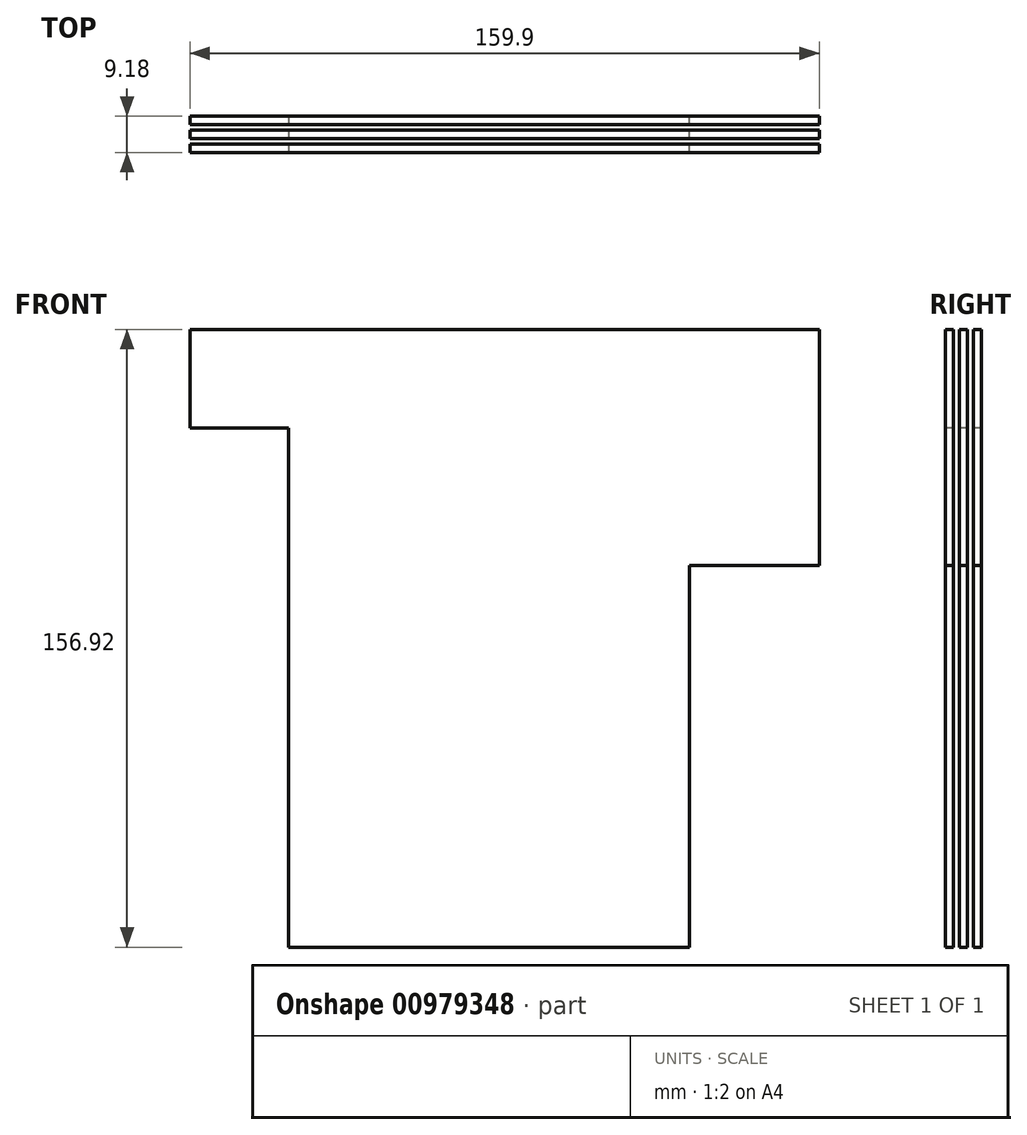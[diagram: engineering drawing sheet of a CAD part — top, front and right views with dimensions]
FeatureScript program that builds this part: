
annotation { "Feature Type Name" : "Feature", "Feature Type Description" : "" }
export const myFeature = defineFeature(function(context is Context, id is Id, definition is map)
    precondition{}
    {
        {
            var Q0;
            Q0=qCreatedBy(makeId("Top.planeOp"),FACE);
            var sketch = newSketch(context, id + "F0", { "sketchPlane" : qUnion([Q0])});
            skLineSegment(sketch, "E0.bottom", {"start": v(50.95, -1.03) * mm, "end": v(-50.95, -1.03) * mm});
            skLineSegment(sketch, "E0.top", {"start": v(50.95, 1.03) * mm, "end": v(-50.95, 1.03) * mm});
            skLineSegment(sketch, "E0.left", {"start": v(50.95, -1.03) * mm, "end": v(50.95, 1.03) * mm});
            skLineSegment(sketch, "E0.right", {"start": v(-50.95, -1.03) * mm, "end": v(-50.95, 1.03) * mm});
            skPoint(sketch, "E0.middle", {"position": v(0, 0) * mm});
            skLineSegment(sketch, "E1.bottom", {"start": v(50.95, 2.53) * mm, "end": v(-50.95, 2.53) * mm});
            skLineSegment(sketch, "E1.top", {"start": v(50.95, 4.6) * mm, "end": v(-50.95, 4.6) * mm});
            skLineSegment(sketch, "E1.left", {"start": v(50.95, 2.53) * mm, "end": v(50.95, 4.6) * mm});
            skLineSegment(sketch, "E1.right", {"start": v(-50.95, 2.53) * mm, "end": v(-50.95, 4.6) * mm});
            skPoint(sketch, "E1.middle", {"position": v(0, 3.56) * mm});
            skLineSegment(sketch, "E2.bottom", {"start": v(50.95, -4.6) * mm, "end": v(-50.95, -4.6) * mm});
            skLineSegment(sketch, "E2.top", {"start": v(50.95, -2.53) * mm, "end": v(-50.95, -2.53) * mm});
            skLineSegment(sketch, "E2.left", {"start": v(50.95, -4.6) * mm, "end": v(50.95, -2.53) * mm});
            skLineSegment(sketch, "E2.right", {"start": v(-50.95, -4.6) * mm, "end": v(-50.95, -2.53) * mm});
            skPoint(sketch, "E2.middle", {"position": v(0, -3.56) * mm});
            skSolve(sketch);
        }
        {
            var Q0;
            Q0 = qSketchRegion(id + "F0", true);
            extrude(context, id + "F1", {"entities" : qUnion([Q0]), "endBound" : BoundingType.SYMMETRIC, "depth" : 156.93 * mm, "offsetDistance" : 25 * mm});
        }
        {
            var Q0;
            Q0=makeQuery(id+"F1.opExtrude","SWEPT_FACE",FACE,{"disambiguationData":[OSD([sQuery(id+"F0.wireOp",EDGE,"E1.right")])]});
            var sketch = newSketch(context, id + "F2", { "sketchPlane" : qUnion([Q0])});
            skLineSegment(sketch, "E3.bottom", {"start": v(-4.6, 78.47) * mm, "end": v(-2.53, 78.47) * mm});
            skLineSegment(sketch, "E3.top", {"start": v(-4.59, 53.47) * mm, "end": v(-2.53, 53.47) * mm});
            skLineSegment(sketch, "E3.left", {"start": v(-4.6, 78.47) * mm, "end": v(-4.6, 53.47) * mm});
            skLineSegment(sketch, "E3.right", {"start": v(-2.53, 78.47) * mm, "end": v(-2.53, 53.47) * mm});
            skSolve(sketch);
        }
        {
            var Q0;
            Q0=makeQuery(id+"F1.opExtrude","SWEPT_FACE",FACE,{"disambiguationData":[OSD([sQuery(id+"F0.wireOp",EDGE,"E0.right")])]});
            var sketch = newSketch(context, id + "F3", { "sketchPlane" : qUnion([Q0])});
            skLineSegment(sketch, "E4.bottom", {"start": v(-1.03, 78.47) * mm, "end": v(1.03, 78.47) * mm});
            skLineSegment(sketch, "E4.top", {"start": v(-1.03, 53.47) * mm, "end": v(1.03, 53.47) * mm});
            skLineSegment(sketch, "E4.left", {"start": v(-1.03, 78.47) * mm, "end": v(-1.03, 53.47) * mm});
            skLineSegment(sketch, "E4.right", {"start": v(1.03, 78.47) * mm, "end": v(1.03, 53.47) * mm});
            skSolve(sketch);
        }
        {
            var Q0;
            Q0=makeQuery(id+"F1.opExtrude","SWEPT_FACE",FACE,{"disambiguationData":[OSD([sQuery(id+"F0.wireOp",EDGE,"E2.right")])]});
            var sketch = newSketch(context, id + "F4", { "sketchPlane" : qUnion([Q0])});
            skLineSegment(sketch, "E5.bottom", {"start": v(2.53, 78.47) * mm, "end": v(4.6, 78.47) * mm});
            skLineSegment(sketch, "E5.top", {"start": v(2.53, 53.47) * mm, "end": v(4.6, 53.47) * mm});
            skLineSegment(sketch, "E5.left", {"start": v(2.53, 78.47) * mm, "end": v(2.53, 53.47) * mm});
            skLineSegment(sketch, "E5.right", {"start": v(4.6, 78.47) * mm, "end": v(4.6, 53.47) * mm});
            skSolve(sketch);
        }
        {
            var Q0;
            Q0=makeQuery(id+"F2.imprint","IMPRINT",FACE,{"disambiguationData":[TD([[makeQuery(id+"F2.imprint","IMPRINT",EDGE,{"derivedFrom":sQuery(id+"F2.wireOp",EDGE,"E3.bottom")}),1.0]])]});
            var Q1;
            Q1=makeQuery(id+"F3.imprint","IMPRINT",FACE,{"disambiguationData":[TD([[makeQuery(id+"F3.imprint","IMPRINT",EDGE,{"derivedFrom":sQuery(id+"F3.wireOp",EDGE,"E4.bottom")}),1.0]])]});
            var Q2;
            Q2=makeQuery(id+"F4.imprint","IMPRINT",FACE,{"disambiguationData":[TD([[makeQuery(id+"F4.imprint","IMPRINT",EDGE,{"derivedFrom":sQuery(id+"F4.wireOp",EDGE,"E5.bottom")}),1.0]])]});
            extrude(context, id + "F5", {"entities" : qUnion([Q0, Q1, Q2]), "operationType" : NewBodyOperationType.ADD, "depth" : 25 * mm, "offsetDistance" : 25 * mm});
        }
        {
            var Q0;
            Q0=makeQuery(id+"F1.opExtrude","SWEPT_FACE",FACE,{"disambiguationData":[OSD([sQuery(id+"F0.wireOp",EDGE,"E2.left")])]});
            var sketch = newSketch(context, id + "F6", { "sketchPlane" : qUnion([Q0])});
            skLineSegment(sketch, "E6.bottom", {"start": v(-4.6, 78.47) * mm, "end": v(-2.53, 78.47) * mm});
            skLineSegment(sketch, "E6.top", {"start": v(-4.6, 18.47) * mm, "end": v(-2.53, 18.47) * mm});
            skLineSegment(sketch, "E6.left", {"start": v(-4.6, 78.47) * mm, "end": v(-4.6, 18.47) * mm});
            skLineSegment(sketch, "E6.right", {"start": v(-2.53, 78.47) * mm, "end": v(-2.53, 18.47) * mm});
            skSolve(sketch);
        }
        {
            var Q0;
            Q0=makeQuery(id+"F1.opExtrude","SWEPT_FACE",FACE,{"disambiguationData":[OSD([sQuery(id+"F0.wireOp",EDGE,"E0.left")])]});
            var sketch = newSketch(context, id + "F7", { "sketchPlane" : qUnion([Q0])});
            skLineSegment(sketch, "E7.bottom", {"start": v(-1.03, 78.47) * mm, "end": v(1.03, 78.47) * mm});
            skLineSegment(sketch, "E7.top", {"start": v(-1.03, 18.47) * mm, "end": v(1.03, 18.47) * mm});
            skLineSegment(sketch, "E7.left", {"start": v(-1.03, 78.47) * mm, "end": v(-1.03, 18.47) * mm});
            skLineSegment(sketch, "E7.right", {"start": v(1.03, 78.47) * mm, "end": v(1.03, 18.47) * mm});
            skSolve(sketch);
        }
        {
            var Q0;
            Q0=makeQuery(id+"F1.opExtrude","SWEPT_FACE",FACE,{"disambiguationData":[OSD([sQuery(id+"F0.wireOp",EDGE,"E1.left")])]});
            var sketch = newSketch(context, id + "F8", { "sketchPlane" : qUnion([Q0])});
            skLineSegment(sketch, "E8.bottom", {"start": v(2.53, 78.47) * mm, "end": v(4.6, 78.47) * mm});
            skLineSegment(sketch, "E8.top", {"start": v(2.53, 18.47) * mm, "end": v(4.6, 18.47) * mm});
            skLineSegment(sketch, "E8.left", {"start": v(2.53, 78.47) * mm, "end": v(2.53, 18.47) * mm});
            skLineSegment(sketch, "E8.right", {"start": v(4.6, 78.47) * mm, "end": v(4.6, 18.47) * mm});
            skSolve(sketch);
        }
        {
            var Q0;
            Q0 = qSketchRegion(id + "F6", true);
            var Q1;
            Q1 = qSketchRegion(id + "F7", true);
            var Q2;
            Q2 = qSketchRegion(id + "F8", true);
            extrude(context, id + "F9", {"entities" : qUnion([Q0, Q1, Q2]), "operationType" : NewBodyOperationType.ADD, "depth" : 33 * mm, "offsetDistance" : 25 * mm});
        }
    });
